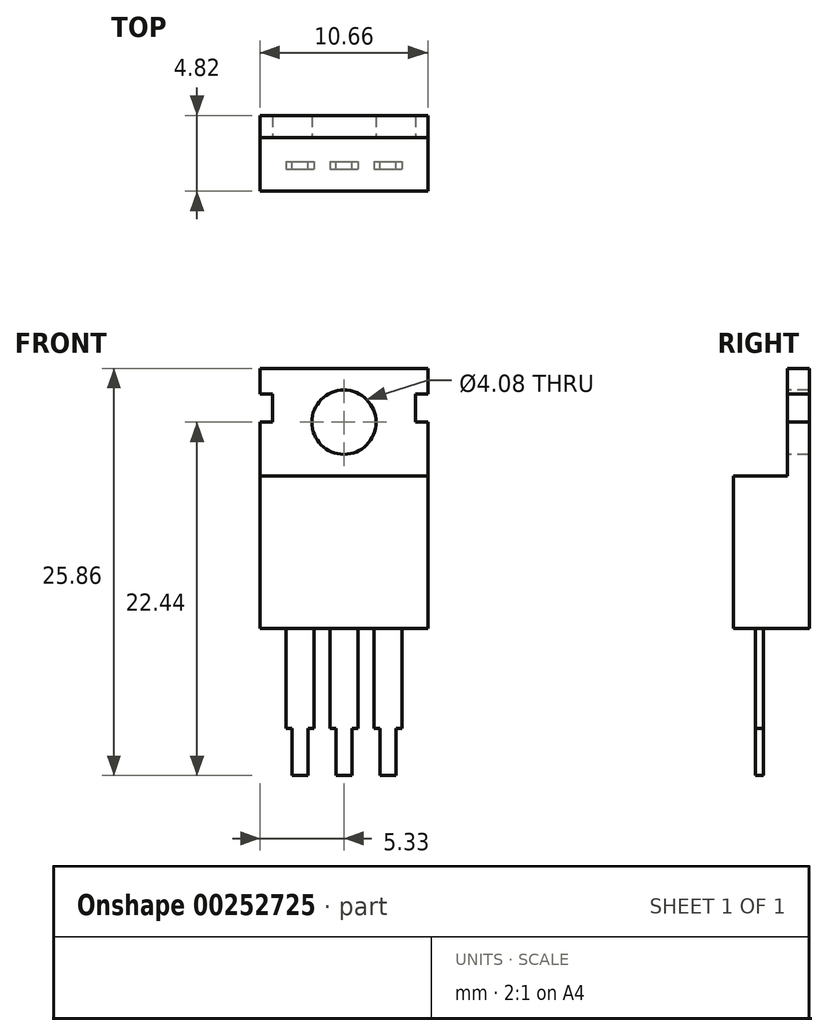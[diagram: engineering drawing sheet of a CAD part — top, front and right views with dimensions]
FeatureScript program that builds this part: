
annotation { "Feature Type Name" : "Feature", "Feature Type Description" : "" }
export const myFeature = defineFeature(function(context is Context, id is Id, definition is map)
    precondition{}
    {
        {
            var Q0;
            Q0=qCreatedBy(makeId("Front.planeOp"),FACE);
            var sketch = newSketch(context, id + "F0", { "sketchPlane" : qUnion([Q0])});
            skLineSegment(sketch, "E0.bottom", {"start": v(-5.33, 16.51) * mm, "end": v(5.33, 16.51) * mm});
            skLineSegment(sketch, "E0.top", {"start": v(-5.33, 0) * mm, "end": v(5.33, 0) * mm});
            skLineSegment(sketch, "E0.left", {"start": v(-5.33, 16.51) * mm, "end": v(-5.33, 0) * mm});
            skLineSegment(sketch, "E0.right", {"start": v(5.33, 16.51) * mm, "end": v(5.33, 0) * mm});
            skCircle(sketch, "E1", {"center": v(0, 13.1) * mm, "radius": 2.04 * mm});
            skLineSegment(sketch, "E2.bottom", {"start": v(-5.33, 14.89) * mm, "end": v(-4.53, 14.89) * mm});
            skLineSegment(sketch, "E2.top", {"start": v(-5.33, 13.1) * mm, "end": v(-4.53, 13.1) * mm});
            skLineSegment(sketch, "E2.left", {"start": v(-5.33, 14.89) * mm, "end": v(-5.33, 13.1) * mm});
            skLineSegment(sketch, "E2.right", {"start": v(-4.53, 14.89) * mm, "end": v(-4.53, 13.1) * mm});
            skLineSegment(sketch, "E3.bottom", {"start": v(5.33, 14.89) * mm, "end": v(4.53, 14.89) * mm});
            skLineSegment(sketch, "E3.top", {"start": v(5.33, 13.1) * mm, "end": v(4.53, 13.1) * mm});
            skLineSegment(sketch, "E3.left", {"start": v(5.33, 14.89) * mm, "end": v(5.33, 13.1) * mm});
            skLineSegment(sketch, "E3.right", {"start": v(4.53, 14.9) * mm, "end": v(4.53, 13.1) * mm});
            skSolve(sketch);
        }
        {
            var Q0;
            Q0=makeQuery(id+"F0.imprint","IMPRINT",FACE,{"disambiguationData":[TD([[makeQuery(id+"F0.imprint","IMPRINT",EDGE,{"derivedFrom":sQuery(id+"F0.wireOp",EDGE,"E0.bottom")}),-1.0]])]});
            extrude(context, id + "F1", {"entities" : qUnion([Q0]), "oppositeDirection" : true, "depth" : 1.4 * mm});
        }
        {
            var Q0;
            Q0=makeQuery(id+"F1.opExtrude","CAP_FACE",FACE,{"disambiguationData":[OSD([sQuery(id+"F0.wireOp",EDGE,"E0.bottom"),sQuery(id+"F0.wireOp",EDGE,"E0.top"),sQuery(id+"F0.wireOp",EDGE,"E0.left"),sQuery(id+"F0.wireOp",EDGE,"E0.right"),sQuery(id+"F0.wireOp",EDGE,"E1")])],"isStart":true});
            var sketch = newSketch(context, id + "F2", { "sketchPlane" : qUnion([Q0])});
            skLineSegment(sketch, "E4.bottom", {"start": v(-5.33, 9.66) * mm, "end": v(5.33, 9.66) * mm});
            skLineSegment(sketch, "E4.top", {"start": v(-5.33, 0) * mm, "end": v(5.33, 0) * mm});
            skLineSegment(sketch, "E4.left", {"start": v(-5.33, 9.66) * mm, "end": v(-5.33, 0) * mm});
            skLineSegment(sketch, "E4.right", {"start": v(5.33, 9.66) * mm, "end": v(5.33, 0) * mm});
            skSolve(sketch);
        }
        {
            var Q0;
            Q0=qSketchRegion(id+"F2",true);
            extrude(context, id + "F3", {"entities" : qUnion([Q0]), "operationType" : NewBodyOperationType.ADD, "depth" : 3.42 * mm});
        }
        {
            var Q0;
            Q0=makeQuery(id+"F3.boolean.opBoolean","MERGE",FACE,{"derivedFrom":[makeQuery(id+"F1.opExtrude","SWEPT_FACE",FACE,{"disambiguationData":[OSD([sQuery(id+"F0.wireOp",EDGE,"E0.top")])]}),makeQuery(id+"F3.opExtrude","SWEPT_FACE",FACE,{"disambiguationData":[OSD([sQuery(id+"F2.wireOp",EDGE,"E4.top")])]})]});
            var sketch = newSketch(context, id + "F4", { "sketchPlane" : qUnion([Q0])});
            skLineSegment(sketch, "E5.bottom", {"start": v(-3.67, 1.52) * mm, "end": v(-1.9, 1.52) * mm});
            skLineSegment(sketch, "E5.top", {"start": v(-3.67, 2.02) * mm, "end": v(-1.9, 2.02) * mm});
            skLineSegment(sketch, "E5.left", {"start": v(-3.67, 1.52) * mm, "end": v(-3.67, 2.02) * mm});
            skLineSegment(sketch, "E5.right", {"start": v(-1.9, 1.52) * mm, "end": v(-1.9, 2.02) * mm});
            skLineSegment(sketch, "E6", {"start": v(0, 4.08) * mm, "end": v(0, -1.89) * mm, "construction": true});
            skPoint(sketch, "E6.startSnap0", {"position": v(0, 3.42) * mm});
            skLineSegment(sketch, "E7", {"start": v(-2.79, 1) * mm, "end": v(-2.79, 2.7) * mm, "construction": true});
            skPoint(sketch, "E7.startSnap0", {"position": v(-2.79, 1.52) * mm});
            skLineSegment(sketch, "E8.1.0.0", {"start": v(0.89, 1.52) * mm, "end": v(0.89, 2.02) * mm});
            skLineSegment(sketch, "E8.1.0.1", {"start": v(-0.88, 2.02) * mm, "end": v(0.89, 2.02) * mm});
            skLineSegment(sketch, "E8.1.0.2", {"start": v(-0.88, 1.52) * mm, "end": v(-0.88, 2.02) * mm});
            skLineSegment(sketch, "E8.1.0.3", {"start": v(-0.88, 1.52) * mm, "end": v(0.89, 1.52) * mm});
            skLineSegment(sketch, "E8.2.0.0", {"start": v(3.68, 1.52) * mm, "end": v(3.68, 2.02) * mm});
            skLineSegment(sketch, "E8.2.0.1", {"start": v(1.9, 2.02) * mm, "end": v(3.68, 2.02) * mm});
            skLineSegment(sketch, "E8.2.0.2", {"start": v(1.9, 1.52) * mm, "end": v(1.9, 2.02) * mm});
            skLineSegment(sketch, "E8.2.0.3", {"start": v(1.9, 1.52) * mm, "end": v(3.68, 1.52) * mm});
            skLineSegment(sketch, "E8.direction1", {"start": v(-1.9, 1.52) * mm, "end": v(0.89, 1.52) * mm, "construction": true});
            skSolve(sketch);
        }
        {
            var Q0;
            Q0=qSketchRegion(id+"F4",true);
            extrude(context, id + "F5", {"entities" : qUnion([Q0]), "operationType" : NewBodyOperationType.ADD, "depth" : 6.35 * mm});
        }
        {
            var Q0;
            Q0=makeQuery(id+"F5.opExtrude","CAP_FACE",FACE,{"disambiguationData":[OSD([sQuery(id+"F4.wireOp",EDGE,"E5.bottom"),sQuery(id+"F4.wireOp",EDGE,"E5.top"),sQuery(id+"F4.wireOp",EDGE,"E5.left"),sQuery(id+"F4.wireOp",EDGE,"E5.right")])],"isStart":false});
            var sketch = newSketch(context, id + "F6", { "sketchPlane" : qUnion([Q0])});
            skLineSegment(sketch, "E9.bottom", {"start": v(-3.3, 2.02) * mm, "end": v(-2.28, 2.02) * mm});
            skLineSegment(sketch, "E9.top", {"start": v(-3.3, 1.52) * mm, "end": v(-2.28, 1.52) * mm});
            skLineSegment(sketch, "E9.left", {"start": v(-3.3, 2.02) * mm, "end": v(-3.3, 1.52) * mm});
            skLineSegment(sketch, "E9.right", {"start": v(-2.28, 2.02) * mm, "end": v(-2.28, 1.52) * mm});
            skLineSegment(sketch, "E10.1.0.0", {"start": v(-0.5, 2.02) * mm, "end": v(0.5, 2.02) * mm});
            skLineSegment(sketch, "E10.1.0.1", {"start": v(0.5, 2.02) * mm, "end": v(0.5, 1.52) * mm});
            skLineSegment(sketch, "E10.1.0.2", {"start": v(-0.5, 1.52) * mm, "end": v(0.5, 1.52) * mm});
            skLineSegment(sketch, "E10.1.0.3", {"start": v(-0.5, 2.02) * mm, "end": v(-0.5, 1.52) * mm});
            skLineSegment(sketch, "E10.2.0.0", {"start": v(2.29, 2.02) * mm, "end": v(3.3, 2.02) * mm});
            skLineSegment(sketch, "E10.2.0.1", {"start": v(3.3, 2.02) * mm, "end": v(3.3, 1.52) * mm});
            skLineSegment(sketch, "E10.2.0.2", {"start": v(2.29, 1.52) * mm, "end": v(3.3, 1.52) * mm});
            skLineSegment(sketch, "E10.2.0.3", {"start": v(2.29, 2.02) * mm, "end": v(2.29, 1.52) * mm});
            skLineSegment(sketch, "E10.direction1", {"start": v(-3.3, 2.02) * mm, "end": v(-0.5, 2.02) * mm, "construction": true});
            skSolve(sketch);
        }
        {
            var Q0;
            Q0=qSketchRegion(id+"F6",true);
            extrude(context, id + "F7", {"entities" : qUnion([Q0]), "operationType" : NewBodyOperationType.ADD, "depth" : 3 * mm});
        }
    });
